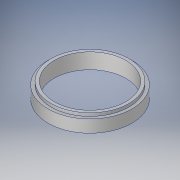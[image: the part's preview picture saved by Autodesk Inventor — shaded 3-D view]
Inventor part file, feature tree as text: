
AUTODESK INVENTOR PART (.ipt)
format: ipt  version: 2017 (Build 210142000, 142)  size: 140,800 bytes
history: native  units: in
note: dims shown in document units (in); Inventor stores cm internally (conversion verified against a paired STEP export)
features: revolve x1, sketch x1
ambient origin geometry x8: Origin, YZ Plane, XZ Plane, XY Plane, X Axis, Y Axis, Z Axis, Center Point
bodies: Body1 (feature_tree)
feature tree (2):
  revolve  "Revolution3"  [1 undecoded]
  sketch  "Sketch1"  dims[d0=0.25in d1=0.1718in d2=15.0deg d4=0.25in d5=1.5in d6=1.25in d7=0.25in d11=0.25in d13=0.5in d15=0.25in d16=0.25in d18=0.125in d19=0.5in d20=0.125in d21=0.25in d22=0.125in d23=0.125in d24=0.25in d25=0.5in d26=2.292in d27=0.5in d29=0.5in d31=90.0deg]
note: 1 required parameter value undecoded (feature->parameter linkage not recoverable at this tier; creation-order binding heuristic only, values carry confidence <= 0.55)
